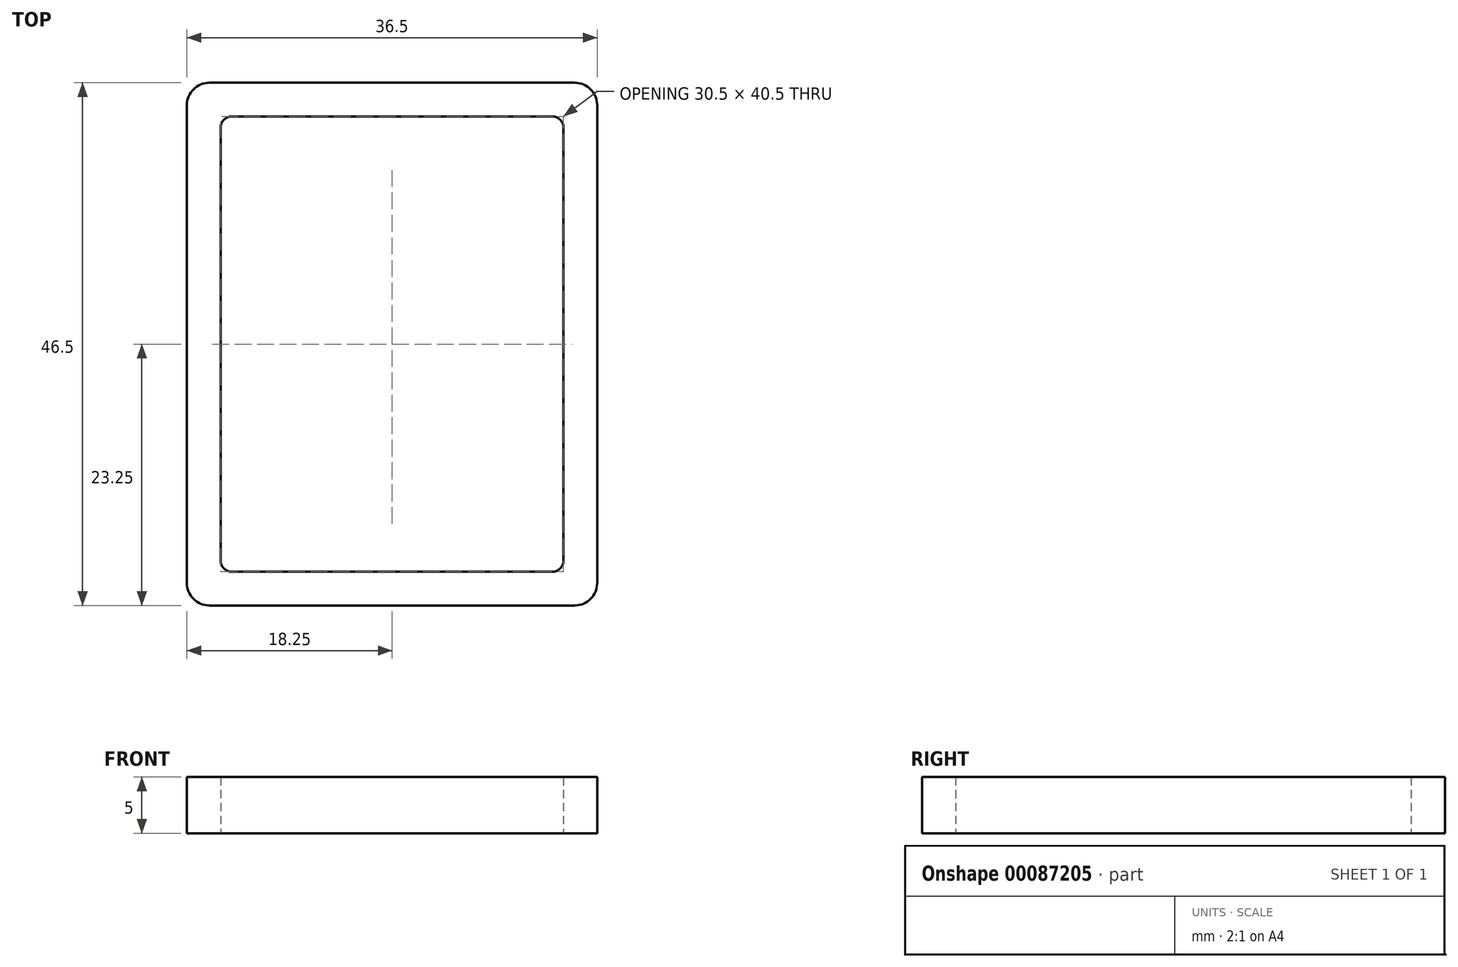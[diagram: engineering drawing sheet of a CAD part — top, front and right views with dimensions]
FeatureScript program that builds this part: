
annotation { "Feature Type Name" : "Feature", "Feature Type Description" : "" }
export const myFeature = defineFeature(function(context is Context, id is Id, definition is map)
    precondition{}
    {
        {
            var Q0;
            Q0=qCreatedBy(makeId("Top.planeOp"),FACE);
            var sketch = newSketch(context, id + "F0", { "sketchPlane" : qUnion([Q0])});
            skLineSegment(sketch, "E0.bottom", {"start": v(15.25, -20.25) * mm, "end": v(-15.25, -20.25) * mm});
            skLineSegment(sketch, "E0.top", {"start": v(15.25, 20.25) * mm, "end": v(-15.25, 20.25) * mm});
            skLineSegment(sketch, "E0.left", {"start": v(15.25, -20.25) * mm, "end": v(15.25, 20.25) * mm});
            skLineSegment(sketch, "E0.right", {"start": v(-15.25, -20.25) * mm, "end": v(-15.25, 20.25) * mm});
            skPoint(sketch, "E0.middle", {"position": v(0, 0) * mm});
            skLineSegment(sketch, "E1.0", {"start": v(18.25, 23.25) * mm, "end": v(-18.25, 23.25) * mm});
            skLineSegment(sketch, "E1.1", {"start": v(18.25, -23.25) * mm, "end": v(18.25, 23.25) * mm});
            skLineSegment(sketch, "E1.2", {"start": v(18.25, -23.25) * mm, "end": v(-18.25, -23.25) * mm});
            skLineSegment(sketch, "E1.3", {"start": v(-18.25, -23.25) * mm, "end": v(-18.25, 23.25) * mm});
            skSolve(sketch);
        }
        {
            var Q0;
            Q0=makeQuery(id+"F0.imprint","IMPRINT",FACE,{"disambiguationData":[TD([[makeQuery(id+"F0.imprint","IMPRINT",EDGE,{"derivedFrom":sQuery(id+"F0.wireOp",EDGE,"E0.bottom")}),1.0]])]});
            extrude(context, id + "F1", {"entities" : qUnion([Q0]), "depth" : 5 * mm});
        }
        {
            var Q0;
            Q0=makeQuery(id+"F1.opExtrude","SWEPT_EDGE",EDGE,{"disambiguationData":[OSD([sQuery(id+"F0.wireOp",EDGE,"E0.top"),sQuery(id+"F0.wireOp",EDGE,"E0.right")])]});
            var Q1;
            Q1=makeQuery(id+"F1.opExtrude","SWEPT_EDGE",EDGE,{"disambiguationData":[OSD([sQuery(id+"F0.wireOp",EDGE,"E0.top"),sQuery(id+"F0.wireOp",EDGE,"E0.left")])]});
            var Q2;
            Q2=makeQuery(id+"F1.opExtrude","SWEPT_EDGE",EDGE,{"disambiguationData":[OSD([sQuery(id+"F0.wireOp",EDGE,"E0.bottom"),sQuery(id+"F0.wireOp",EDGE,"E0.right")])]});
            var Q3;
            Q3=makeQuery(id+"F1.opExtrude","SWEPT_EDGE",EDGE,{"disambiguationData":[OSD([sQuery(id+"F0.wireOp",EDGE,"E0.bottom"),sQuery(id+"F0.wireOp",EDGE,"E0.left")])]});
            fillet(context, id + "F2", {"entities" : qUnion([Q0, Q1, Q2, Q3]), "radius" : 1 * mm, "tangentPropagation" : true, "allowEdgeOverflow" : false});
        }
        {
            var Q0;
            Q0=makeQuery(id+"F1.opExtrude","SWEPT_EDGE",EDGE,{"disambiguationData":[OSD([sQuery(id+"F0.wireOp",EDGE,"E1.1"),sQuery(id+"F0.wireOp",EDGE,"E1.2")])]});
            var Q1;
            Q1=makeQuery(id+"F1.opExtrude","SWEPT_EDGE",EDGE,{"disambiguationData":[OSD([sQuery(id+"F0.wireOp",EDGE,"E1.0"),sQuery(id+"F0.wireOp",EDGE,"E1.1")])]});
            var Q2;
            Q2=makeQuery(id+"F1.opExtrude","SWEPT_EDGE",EDGE,{"disambiguationData":[OSD([sQuery(id+"F0.wireOp",EDGE,"E1.0"),sQuery(id+"F0.wireOp",EDGE,"E1.3")])]});
            var Q3;
            Q3=makeQuery(id+"F1.opExtrude","SWEPT_EDGE",EDGE,{"disambiguationData":[OSD([sQuery(id+"F0.wireOp",EDGE,"E1.2"),sQuery(id+"F0.wireOp",EDGE,"E1.3")])]});
            fillet(context, id + "F3", {"entities" : qUnion([Q0, Q1, Q2, Q3]), "radius" : 2 * mm, "tangentPropagation" : true, "allowEdgeOverflow" : false});
        }
    });
